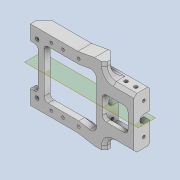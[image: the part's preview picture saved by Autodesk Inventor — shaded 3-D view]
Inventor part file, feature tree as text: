
AUTODESK INVENTOR PART (.ipt)
format: ipt  version: 2020 (Build 240168000, 168)  size: 620,032 bytes
history: native  units: mm
features: extrude x14, sketch x14, projected_geometry x14, thicken_offset x9, fillet x8, reference x5, other x5, mirror x3, chamfer x3, plane x2
ambient origin geometry x8: Origin, YZ Plane, XZ Plane, XY Plane, X Axis, Y Axis, Z Axis, Center Point
bodies: Solid1 (feature_tree)
feature tree (77):
  extrude  "Extrusion1"  Depth=7.0mm
  thicken_offset  "Thicken1"
  thicken_offset  "Thicken2"
  thicken_offset  "Thicken3"
  thicken_offset  "Thicken4"
  extrude  "Extrusion2"  Depth=7.0mm
  thicken_offset  "Thicken5"
  thicken_offset  "Thicken6"
  thicken_offset  "Thicken7"
  extrude  "Extrusion3"  Depth=21.0mm
  extrude  "Extrusion4"  Depth=4.0mm
  extrude  "Extrusion5"  Depth=4.0mm
  extrude  "Extrusion6"  Depth=15.0mm
  extrude  "Extrusion7"  Depth=15.0mm
  extrude  "Extrusion8"  Depth=4.0mm
  extrude  "Extrusion9"  Depth=3.0mm TaperAngle=0.0deg
  extrude  "Extrusion10"  Depth=1.0mm
  fillet  "Fillet1"  Radius=1.0mm
  fillet  "Fillet2"  Radius=1.0mm
  fillet  "Fillet3"  Radius=1.0mm
  fillet  "Fillet4"  Radius=1.0mm
  fillet  "Fillet5"  Radius=1.0mm
  sketch  "Sketch11"  dims[d27=1.0mm d28=7.5mm]
  plane  "Work Plane1"
  extrude  "Extrusion11"  Depth=7.5mm
  plane  "Work Plane2"
  mirror  "Mirror1"
  extrude  "Extrusion12"  Depth=15.0mm
  extrude  "Extrusion13"  Depth=4.0mm
  mirror  "Mirror2"
  extrude  "Extrusion15"  Depth=2.0mm
  mirror  "Mirror3"
  chamfer  "Chamfer1"  Distance=1.0mm
  fillet  "Fillet6"  Radius=1.0mm
  fillet  "Fillet7"  Radius=1.0mm
  chamfer  "Chamfer2"  Distance=1.0mm
  fillet  "Fillet8"  Radius=1.0mm
  chamfer  "Chamfer3"  Distance=1.5mm
  thicken_offset  "Thicken8"
  thicken_offset  "Thicken9"
  sketch  "Sketch1"  dims[d0=5.0mm d1=7.0mm]
  reference  "Reference1"
  reference  "Reference2"
  reference  "Reference3"
  sketch  "Sketch2"  dims[d2=5.0mm d3=7.0mm]
  projected_geometry  "Projected Loop1"
  sketch  "Sketch3"  dims[d4=3.0mm d5=21.0mm]
  projected_geometry  "Projected Loop2"
  sketch  "Sketch4"  dims[d6=12.0mm d7=4.0mm]
  projected_geometry  "Projected Loop3"
  sketch  "Sketch5"  dims[d8=12.0mm d9=4.0mm]
  projected_geometry  "Projected Loop4"
  sketch  "Sketch6"  dims[d10=15.0mm d11=1.745329mm]
  reference  "Reference4"
  reference  "Reference5"
  sketch  "Sketch7"  dims[d12=4.0mm d13=15.0mm]
  sketch  "Sketch8"  dims[d14=1.745329mm d15=4.0mm]
  projected_geometry  "Projected Loop5"
  projected_geometry  "Projected Loop6"
  projected_geometry  "Projected Loop7"
  projected_geometry  "Projected Loop8"
  sketch  "Sketch9"  dims[d16=3.0mm d18=3.0mm d19=0.0mm]
  projected_geometry  "Projected Loop9"
  sketch  "Sketch10"  dims[d20=1.0mm d21=1.0mm d22=1.0mm d23=1.0mm d24=1.0mm d25=1.0mm d26=1.0mm]
  projected_geometry  "Projected Loop10"
  projected_geometry  "Projected Loop11"
  sketch  "Sketch12"  dims[d29=12.0mm d30=15.0mm]
  projected_geometry  "Projected Loop12"
  sketch  "Sketch13"  dims[d31=4.0mm d32=4.0mm]
  projected_geometry  "Projected Loop13"
  sketch  "Sketch15"  dims[d33=3.0mm d34=0.0mm d35=1.0mm d36=1.0mm d37=1.0mm d38=1.0mm d39=1.0mm d40=1.0mm d41=1.5mm d42=3.0mm d43=20.0mm d44=5.0mm d45=0.0mm d46=1.5mm d47=3.0mm d48=20.0mm d49=5.0mm d50=0.0mm d51=36.0mm d52=12.0mm d53=5.0mm d54=0.0mm d55=50.0mm d56=0.0mm d57=5.0mm d58=4.0mm d59=50.0mm d60=0.0mm d61=19.0mm d62=3.0mm d63=19.0mm d64=3.0mm d65=50.0mm d66=0.0mm d67=50.0mm d68=0.0mm d69=13.0mm d70=4.0mm d71=13.0mm d72=4.0mm d73=2.0mm d74=0.0mm d75=2.0mm d76=3.0mm d77=3.0mm d78=2.0mm d79=4.5mm d80=1.5mm d81=1.5mm d82=1.5mm d83=2.0mm d84=0.0mm d85=8.0mm d86=1.8mm d87=40.0mm d88=0.0mm d89=2.5mm d90=1.4mm d91=8.0mm d92=6.0mm d93=1.4mm d94=1.4mm d95=40.0mm d96=0.0mm d103=3.0mm d104=1.8mm d105=3.0mm d106=0.0mm d107=4.0mm d108=2.0mm d109=45.0deg d110=1.0mm d111=1.0mm d112=1.5mm d113=2.0mm d114=45.0deg d115=2.0mm d116=1.0mm d117=2.0mm d118=45.0deg d120=0.05mm d121=0.05mm d122=0.05mm d123=0.05mm]
  projected_geometry  "Projected Loop15"
  parser-record x1  (decoder bookkeeping rows leaked as tree rows — omitted from the tree; the rows remain in map.json)
  other  "tip_3_n_ass.iam"
  other  "end_shell_n_1:1"
  other  "bearing_hh_1:2"
  other  "bearing_hh_1:1"
note: 1 file-system path scrubbed to <path> (originals preserved in map.json)
